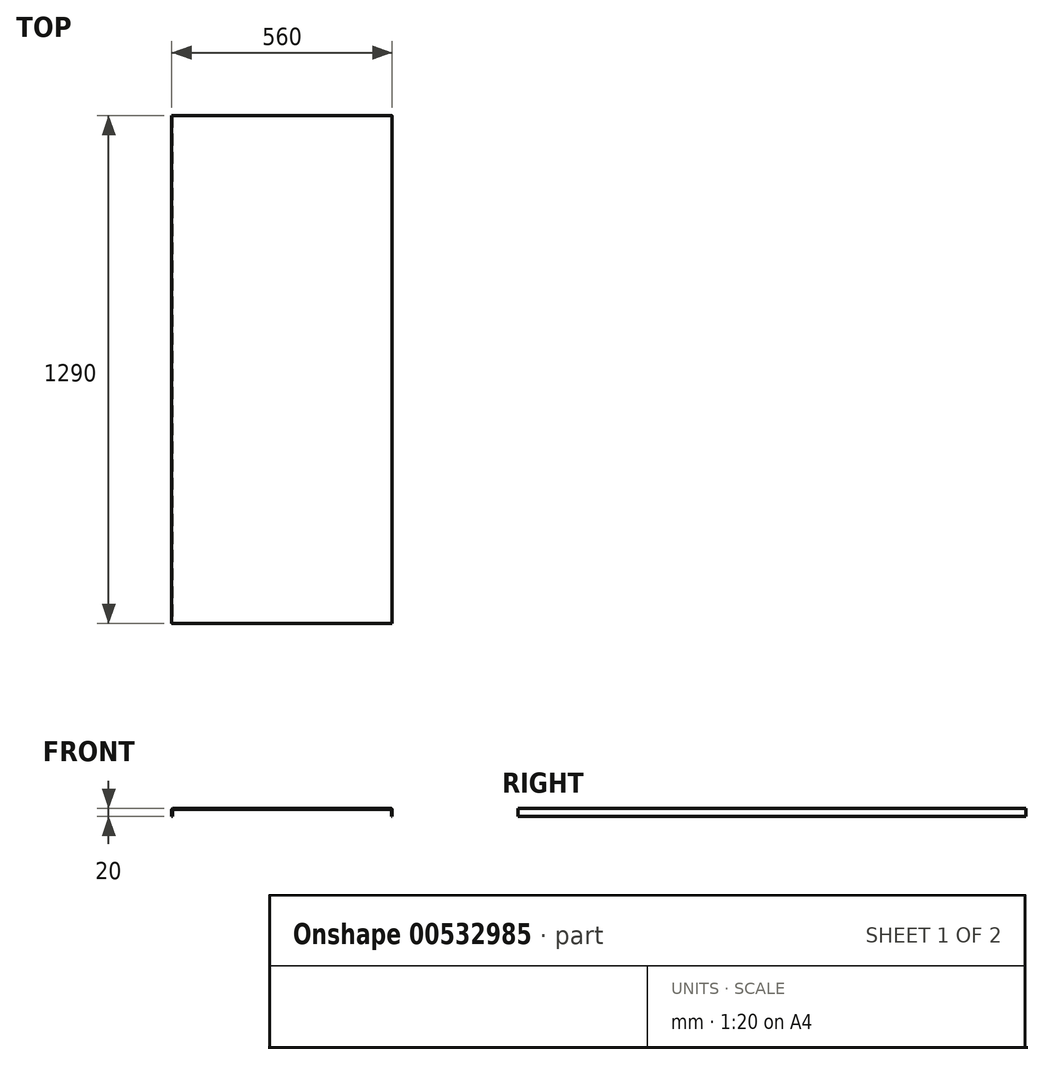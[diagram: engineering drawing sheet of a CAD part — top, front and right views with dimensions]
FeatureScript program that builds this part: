
annotation { "Feature Type Name" : "Feature", "Feature Type Description" : "" }
export const myFeature = defineFeature(function(context is Context, id is Id, definition is map)
    precondition{}
    {
        {
            var Q0;
            Q0=qCreatedBy(makeId("Front.planeOp"),FACE);
            var sketch = newSketch(context, id + "F0", { "sketchPlane" : qUnion([Q0])});
            skLineSegment(sketch, "E0", {"start": v(-96.54, 0) * mm, "end": v(-96.54, 16) * mm});
            skLineSegment(sketch, "E1", {"start": v(-92.54, 20) * mm, "end": v(459.46, 20) * mm});
            skLineSegment(sketch, "E2", {"start": v(463.46, 16) * mm, "end": v(463.46, 0) * mm});
            skLineSegment(sketch, "E3.0", {"start": v(-94.54, 0) * mm, "end": v(-94.54, 16) * mm});
            skLineSegment(sketch, "E4.0", {"start": v(-92.54, 18) * mm, "end": v(459.46, 18) * mm});
            skLineSegment(sketch, "E5.0", {"start": v(461.46, 16) * mm, "end": v(461.46, 0) * mm});
            skLineSegment(sketch, "E6", {"start": v(-94.54, 0) * mm, "end": v(-96.54, 0) * mm});
            skPoint(sketch, "E7.visualSharp", {"position": v(-96.54, 20) * mm});
            skArc(sketch, "E7.filletArc", {"start": v(-92.54, 20) * mm, "mid": v(-95.37, 18.83) * mm, "end": v(-96.54, 16) * mm});
            skPoint(sketch, "E8.visualSharp", {"position": v(-94.54, 18) * mm});
            skArc(sketch, "E8.filletArc", {"start": v(-92.54, 18) * mm, "mid": v(-93.95, 17.41) * mm, "end": v(-94.54, 16) * mm});
            skPoint(sketch, "E9.visualSharp", {"position": v(461.46, 18) * mm});
            skArc(sketch, "E9.filletArc", {"start": v(461.46, 16) * mm, "mid": v(460.88, 17.41) * mm, "end": v(459.46, 18) * mm});
            skPoint(sketch, "E10.visualSharp", {"position": v(463.46, 20) * mm});
            skArc(sketch, "E10.filletArc", {"start": v(463.46, 16) * mm, "mid": v(462.29, 18.83) * mm, "end": v(459.46, 20) * mm});
            skLineSegment(sketch, "E11", {"start": v(463.46, 0) * mm, "end": v(461.46, 0) * mm});
            skSolve(sketch);
        }
        {
            var Q0;
            Q0=makeQuery(id+"F0.imprint","IMPRINT",FACE,{"disambiguationData":[TD([[makeQuery(id+"F0.imprint","IMPRINT",EDGE,{"derivedFrom":sQuery(id+"F0.wireOp",EDGE,"E0")}),-1.0]])]});
            extrude(context, id + "F1", {"entities" : qUnion([Q0]), "oppositeDirection" : true, "depth" : 1290 * mm, "offsetDistance" : 25 * mm});
        }
    });
